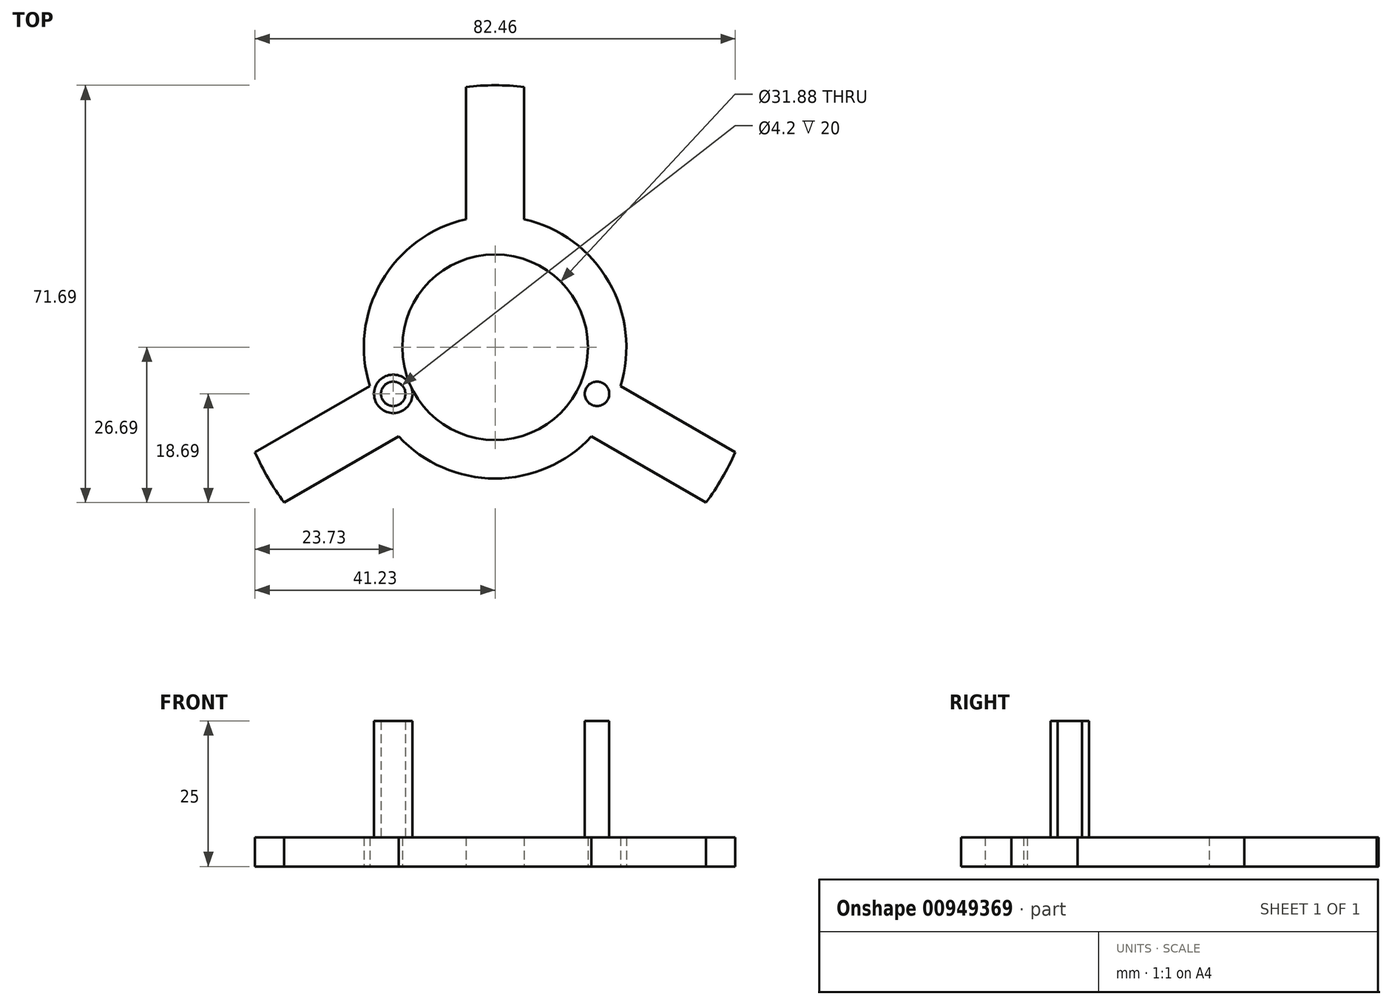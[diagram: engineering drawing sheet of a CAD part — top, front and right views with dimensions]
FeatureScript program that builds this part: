
annotation { "Feature Type Name" : "Feature", "Feature Type Description" : "" }
export const myFeature = defineFeature(function(context is Context, id is Id, definition is map)
    precondition{}
    {
        {
            var Q0;
            Q0=qCreatedBy(makeId("Top.planeOp"),FACE);
            var sketch = newSketch(context, id + "F0", { "sketchPlane" : qUnion([Q0])});
            skCircle(sketch, "E0", {"center": v(-17.5, -8) * mm, "radius": 2.1 * mm});
            skCircle(sketch, "E1", {"center": v(-17.5, -8) * mm, "radius": 3.3 * mm});
            skCircle(sketch, "E2", {"center": v(0, 0) * mm, "radius": 4.5 * mm});
            skCircle(sketch, "E3.MirrorC", {"center": v(17.5, -8) * mm, "radius": 3.3 * mm});
            skCircle(sketch, "E4.MirrorC", {"center": v(17.5, -8) * mm, "radius": 2.1 * mm});
            skCircle(sketch, "E5", {"center": v(0, 0) * mm, "radius": 2.5 * mm});
            skCircle(sketch, "E6", {"center": v(0, 0) * mm, "radius": 1.5 * mm, "construction": true});
            skLineSegment(sketch, "E7", {"start": v(1.5, 2) * mm, "end": v(1.5, -2) * mm});
            skLineSegment(sketch, "E8", {"start": v(-1.5, 2) * mm, "end": v(-1.5, -2) * mm});
            skLineSegment(sketch, "E9", {"start": v(0, 0) * mm, "end": v(0, -2.5) * mm, "construction": true});
            skCircle(sketch, "E10", {"center": v(0, 0) * mm, "radius": 50 * mm});
            skCircle(sketch, "E11", {"center": v(0, 0) * mm, "radius": 45 * mm});
            skCircle(sketch, "E12", {"center": v(0, 0) * mm, "radius": 22.54 * mm});
            skLineSegment(sketch, "E13", {"start": v(5, 21.98) * mm, "end": v(5, 44.72) * mm});
            skLineSegment(sketch, "E14", {"start": v(-5, 44.72) * mm, "end": v(-5, 21.98) * mm});
            skLineSegment(sketch, "E15.1.0", {"start": v(41.23, -18.03) * mm, "end": v(21.54, -6.66) * mm});
            skLineSegment(sketch, "E15.1.1", {"start": v(16.54, -15.32) * mm, "end": v(36.23, -26.7) * mm});
            skLineSegment(sketch, "E15.2.0", {"start": v(-36.23, -26.7) * mm, "end": v(-16.54, -15.32) * mm});
            skLineSegment(sketch, "E15.2.1", {"start": v(-21.54, -6.66) * mm, "end": v(-41.23, -18.03) * mm});
            skLineSegment(sketch, "E15.anchor1", {"start": v(0, 0) * mm, "end": v(-5, 21.98) * mm, "construction": true});
            skLineSegment(sketch, "E15.anchor2", {"start": v(0, 0) * mm, "end": v(-16.54, -15.32) * mm, "construction": true});
            skCircle(sketch, "E16", {"center": v(0, 0) * mm, "radius": 15.94 * mm});
            skSolve(sketch);
        }
        {
            var Q0;
            {var subQ0=sQuery(id+"F0.wireOp",EDGE,"E15.2.0");Q0=makeQuery(id+"F0.imprint","IMPRINT",FACE,{"disambiguationData":[TD([[makeQuery(id+"F0.imprint","IMPRINT",EDGE,{"derivedFrom":subQ0}),1.0]])]});}
            var Q1;
            {var subQ0=sQuery(id+"F0.wireOp",EDGE,"E13");Q1=makeQuery(id+"F0.imprint","IMPRINT",FACE,{"disambiguationData":[TD([[makeQuery(id+"F0.imprint","IMPRINT",EDGE,{"derivedFrom":subQ0}),1.0]])]});}
            var Q2;
            {var subQ0=sQuery(id+"F0.wireOp",EDGE,"E15.1.0");Q2=makeQuery(id+"F0.imprint","IMPRINT",FACE,{"disambiguationData":[TD([[makeQuery(id+"F0.imprint","IMPRINT",EDGE,{"derivedFrom":subQ0}),1.0]])]});}
            var Q3;
            {var subQ0=sQuery(id+"F0.wireOp",EDGE,"E12");var subQ3=sQuery(id+"F0.wireOp",EDGE,"E1");var subQ4=makeQuery(id+"F0.imprint","INTERSECT",VERTEX,{"derivedFrom":[subQ3,subQ0]});Q3=makeQuery(id+"F0.imprint","IMPRINT",FACE,{"disambiguationData":[TD([[makeQuery(id+"F0.imprint","IMPRINT",EDGE,{"disambiguationData":[TD([[subQ4,-1.0]])],"derivedFrom":subQ3}),-1.0]])]});}
            var Q4;
            Q4=makeQuery(id+"F0.imprint","IMPRINT",FACE,{"disambiguationData":[TD([[makeQuery(id+"F0.imprint","IMPRINT",EDGE,{"derivedFrom":sQuery(id+"F0.wireOp",EDGE,"E4.MirrorC")}),1.0]])]});
            var Q5;
            Q5=makeQuery(id+"F0.imprint","IMPRINT",FACE,{"disambiguationData":[TD([[makeQuery(id+"F0.imprint","IMPRINT",EDGE,{"derivedFrom":sQuery(id+"F0.wireOp",EDGE,"E4.MirrorC")}),-1.0]])]});
            var Q6;
            {var subQ0=sQuery(id+"F0.wireOp",EDGE,"E12");var subQ9=sQuery(id+"F0.wireOp",EDGE,"E1");var subQ10=makeQuery(id+"F0.imprint","INTERSECT",VERTEX,{"derivedFrom":[subQ9,subQ0]});Q6=makeQuery(id+"F0.imprint","IMPRINT",FACE,{"disambiguationData":[TD([[makeQuery(id+"F0.imprint","IMPRINT",EDGE,{"disambiguationData":[TD([[subQ10,1.0]])],"derivedFrom":subQ9}),-1.0]])]});}
            var Q7;
            Q7=makeQuery(id+"F0.imprint","IMPRINT",FACE,{"disambiguationData":[TD([[makeQuery(id+"F0.imprint","IMPRINT",EDGE,{"derivedFrom":sQuery(id+"F0.wireOp",EDGE,"E0")}),-1.0]])]});
            var Q8;
            Q8=makeQuery(id+"F0.imprint","IMPRINT",FACE,{"disambiguationData":[TD([[makeQuery(id+"F0.imprint","IMPRINT",EDGE,{"derivedFrom":sQuery(id+"F0.wireOp",EDGE,"E0")}),1.0]])]});
            extrude(context, id + "F1", {"entities" : qUnion([Q0, Q1, Q2, Q3, Q4, Q5, Q6, Q7, Q8]), "depth" : 5 * mm, "offsetDistance" : 25 * mm});
        }
        {
            var Q0;
            Q0=makeQuery(id+"F0.imprint","IMPRINT",FACE,{"disambiguationData":[TD([[makeQuery(id+"F0.imprint","IMPRINT",EDGE,{"derivedFrom":sQuery(id+"F0.wireOp",EDGE,"E0")}),-1.0]])]});
            var Q1;
            Q1=makeQuery(id+"F0.imprint","IMPRINT",FACE,{"disambiguationData":[TD([[makeQuery(id+"F0.imprint","IMPRINT",EDGE,{"derivedFrom":sQuery(id+"F0.wireOp",EDGE,"E4.MirrorC")}),1.0]])]});
            extrude(context, id + "F2", {"entities" : qUnion([Q0, Q1]), "operationType" : NewBodyOperationType.ADD, "depth" : 25 * mm, "offsetDistance" : 25 * mm});
        }
    });
